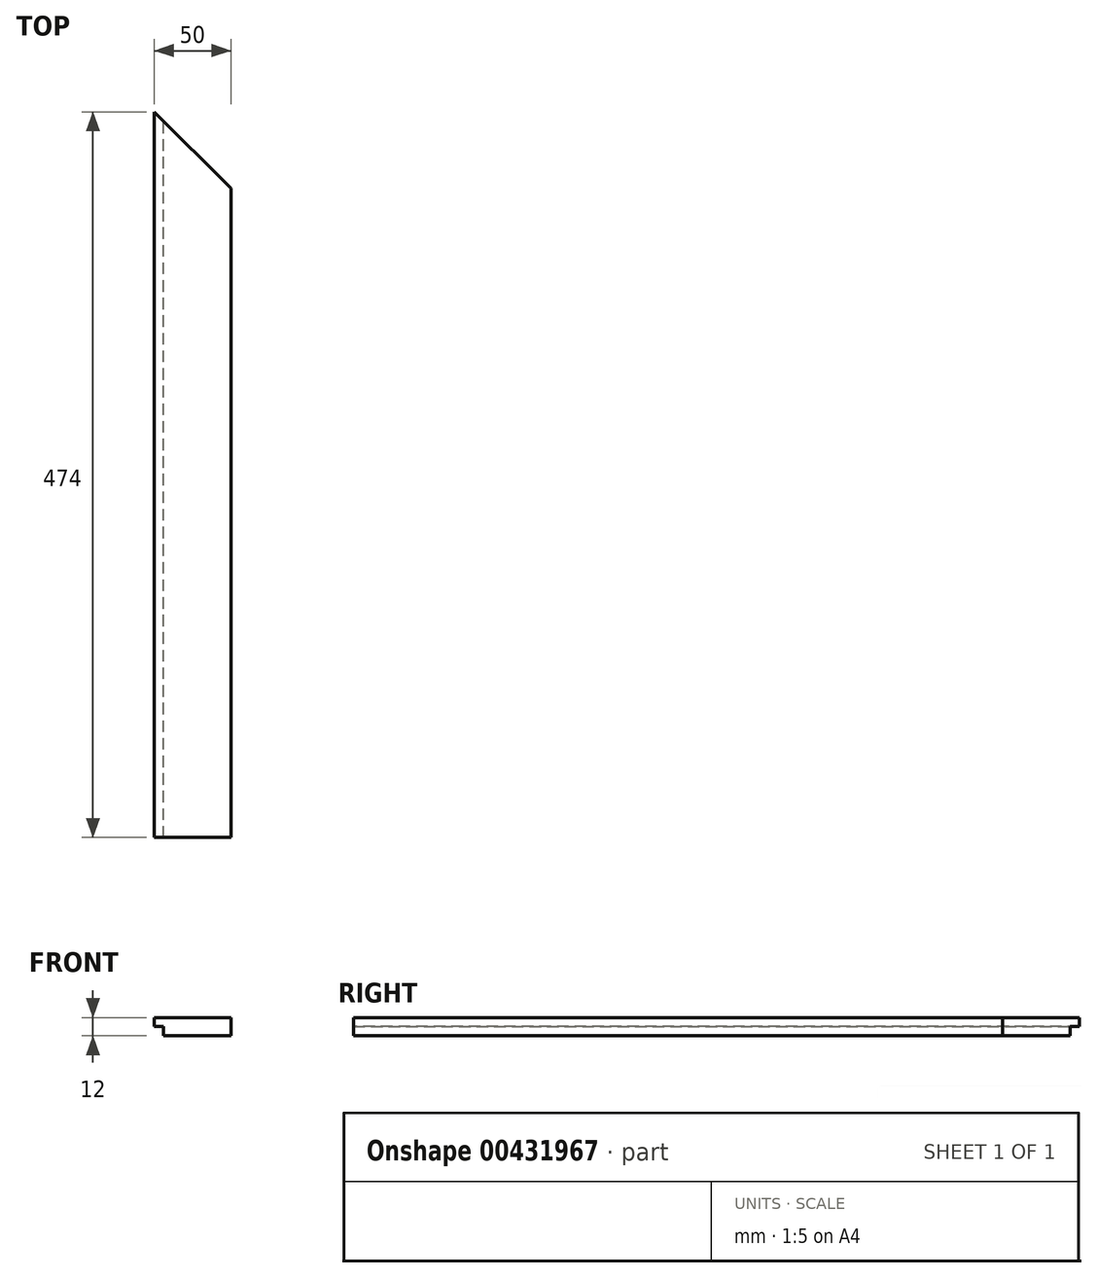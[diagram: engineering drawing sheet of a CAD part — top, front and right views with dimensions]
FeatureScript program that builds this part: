
annotation { "Feature Type Name" : "Feature", "Feature Type Description" : "" }
export const myFeature = defineFeature(function(context is Context, id is Id, definition is map)
    precondition{}
    {
        {
            var Q0;
            Q0=qCreatedBy(makeId("Top.planeOp"),FACE);
            var sketch = newSketch(context, id + "F0", { "sketchPlane" : qUnion([Q0])});
            skLineSegment(sketch, "E0.bottom", {"start": v(-25, 237) * mm, "end": v(25, 237) * mm});
            skLineSegment(sketch, "E0.top", {"start": v(-25, -237) * mm, "end": v(25, -237) * mm});
            skLineSegment(sketch, "E0.left", {"start": v(-25, 237) * mm, "end": v(-25, -237) * mm});
            skLineSegment(sketch, "E0.right", {"start": v(25, 237) * mm, "end": v(25, -237) * mm});
            skPoint(sketch, "E0.middle", {"position": v(0, 0) * mm});
            skSolve(sketch);
        }
        {
            var Q0;
            Q0=qSketchRegion(id+"F0",true);
            extrude(context, id + "F1", {"entities" : qUnion([Q0]), "depth" : 12 * mm, "offsetDistance" : 25 * mm});
        }
        {
            var Q0;
            Q0=makeQuery(id+"F1.opExtrude","CAP_FACE",FACE,{"disambiguationData":[OSD([sQuery(id+"F0.wireOp",EDGE,"E0.bottom"),sQuery(id+"F0.wireOp",EDGE,"E0.top"),sQuery(id+"F0.wireOp",EDGE,"E0.left"),sQuery(id+"F0.wireOp",EDGE,"E0.right")])],"isStart":true});
            var sketch = newSketch(context, id + "F2", { "sketchPlane" : qUnion([Q0])});
            skLineSegment(sketch, "E1.bottom", {"start": v(-25, 237) * mm, "end": v(-19, 237) * mm});
            skLineSegment(sketch, "E1.top", {"start": v(-25, -237) * mm, "end": v(-19, -237) * mm});
            skLineSegment(sketch, "E1.left", {"start": v(-25, 237) * mm, "end": v(-25, -237) * mm});
            skLineSegment(sketch, "E1.right", {"start": v(-19, 237) * mm, "end": v(-19, -237) * mm});
            skSolve(sketch);
        }
        {
            var Q0;
            Q0=qSketchRegion(id+"F2",true);
            extrude(context, id + "F3", {"entities" : qUnion([Q0]), "operationType" : NewBodyOperationType.REMOVE, "oppositeDirection" : true, "depth" : 6 * mm, "offsetDistance" : 25 * mm});
        }
        {
            var Q0;
            Q0=makeQuery(id+"F1.opExtrude","CAP_FACE",FACE,{"disambiguationData":[OSD([sQuery(id+"F0.wireOp",EDGE,"E0.bottom"),sQuery(id+"F0.wireOp",EDGE,"E0.top"),sQuery(id+"F0.wireOp",EDGE,"E0.left"),sQuery(id+"F0.wireOp",EDGE,"E0.right")])],"isStart":false});
            var sketch = newSketch(context, id + "F4", { "sketchPlane" : qUnion([Q0])});
            skLineSegment(sketch, "E2", {"start": v(-25, 237) * mm, "end": v(25, 187) * mm});
            skLineSegment(sketch, "E3", {"start": v(25, 187) * mm, "end": v(25, 237) * mm});
            skLineSegment(sketch, "E4", {"start": v(25, 237) * mm, "end": v(-25, 237) * mm});
            skSolve(sketch);
        }
        {
            var Q0;
            Q0=qSketchRegion(id+"F4",true);
            extrude(context, id + "F5", {"entities" : qUnion([Q0]), "operationType" : NewBodyOperationType.REMOVE, "endBound" : BoundingType.UP_TO_NEXT, "oppositeDirection" : true, "depth" : 25 * mm});
        }
    });
